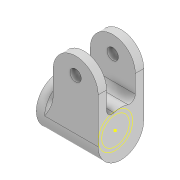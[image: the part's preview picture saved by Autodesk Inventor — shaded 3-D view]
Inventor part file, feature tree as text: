
AUTODESK INVENTOR PART (.ipt)
format: ipt  version: 2022 (Build 260153000, 153)  size: 178,176 bytes
history: native  units: mm
features: sketch x5, extrude x4, fillet x2, projected_geometry x2
ambient origin geometry x8: Origin, YZ Plane, XZ Plane, XY Plane, X Axis, Y Axis, Z Axis, Center Point
bodies: Solid1 (feature_tree)
feature tree (13):
  extrude  "Extrusion1"  Depth=12.2mm
  extrude  "Extrusion2"  Depth=2.0mm TaperAngle=0.0deg
  sketch  "Sketch5"  dims[d5=2.0mm d6=0.0mm d23=16.0mm]
  sketch  "Sketch6"  dims[d24=5.1mm d25=5.1mm d26=3.0mm d27=3.0mm]
  extrude  "Extrusion5"  Depth=2.0mm
  extrude  "Extrusion6"  Depth=5.1mm
  fillet  "Fillet2"  Radius=3.0mm
  fillet  "Fillet3"  Radius=3.0mm
  sketch  "Sketch1"  dims[d0=9.8mm d1=12.2mm]
  sketch  "Sketch2"  dims[d2=2.0mm d3=20.0mm d4=0.0mm]
  projected_geometry  "Projected Loop1"
  projected_geometry  "Projected Loop2"
  sketch  "Sketch7"  dims[d28=24.0mm d29=0.0mm d30=4.0mm d31=6.0mm d32=8.0mm d33=100.0mm d34=0.0mm d35=3.0mm d36=2.0mm]
